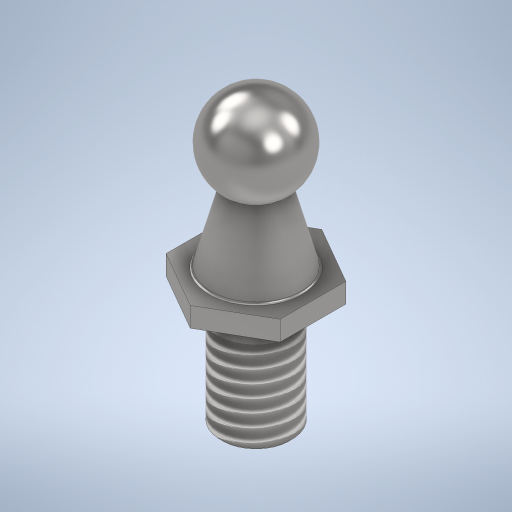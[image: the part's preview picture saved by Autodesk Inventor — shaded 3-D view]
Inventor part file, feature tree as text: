
AUTODESK INVENTOR PART (.ipt)
format: ipt  version: 2024 (Build 280153000, 153)  size: 348,160 bytes
history: native  units: mm
features: fillet x2, sketch x2, revolve x1, extrude x1, chamfer x1, thread x1, projected_geometry x1
ambient origin geometry x8: Origin, YZ Plane, XZ Plane, XY Plane, X Axis, Y Axis, Z Axis, Center Point
bodies: Solid1 (feature_tree)
feature tree (9):
  revolve  "Revolution1"  [1 undecoded]
  extrude  "Extrusion1"  Depth=10.0mm
  chamfer  "Chamfer1"  Distance=12.7mm
  fillet  "Fillet1"  [1 undecoded]
  fillet  "Fillet2"  Radius=2.2mm
  thread  "Thread1"  [1 undecoded]
  sketch  "Sketch1"  dims[d0=10.0mm d1=7.9375mm]
  sketch  "Sketch2"  dims[d2=32.0mm d3=20.0mm d4=12.7mm d5=30.0deg d6=2.2mm d7=90.0deg d8=12.7mm d9=0.0mm d10=0.0mm d11=0.25mm d12=2.0mm d13=45.0deg d14=0.25mm d15=0.25mm d16=10.0mm d17=0.0mm]
  projected_geometry  "Projected Loop1"
note: 3 required parameter values undecoded (feature->parameter linkage not recoverable at this tier; creation-order binding heuristic only, values carry confidence <= 0.55)